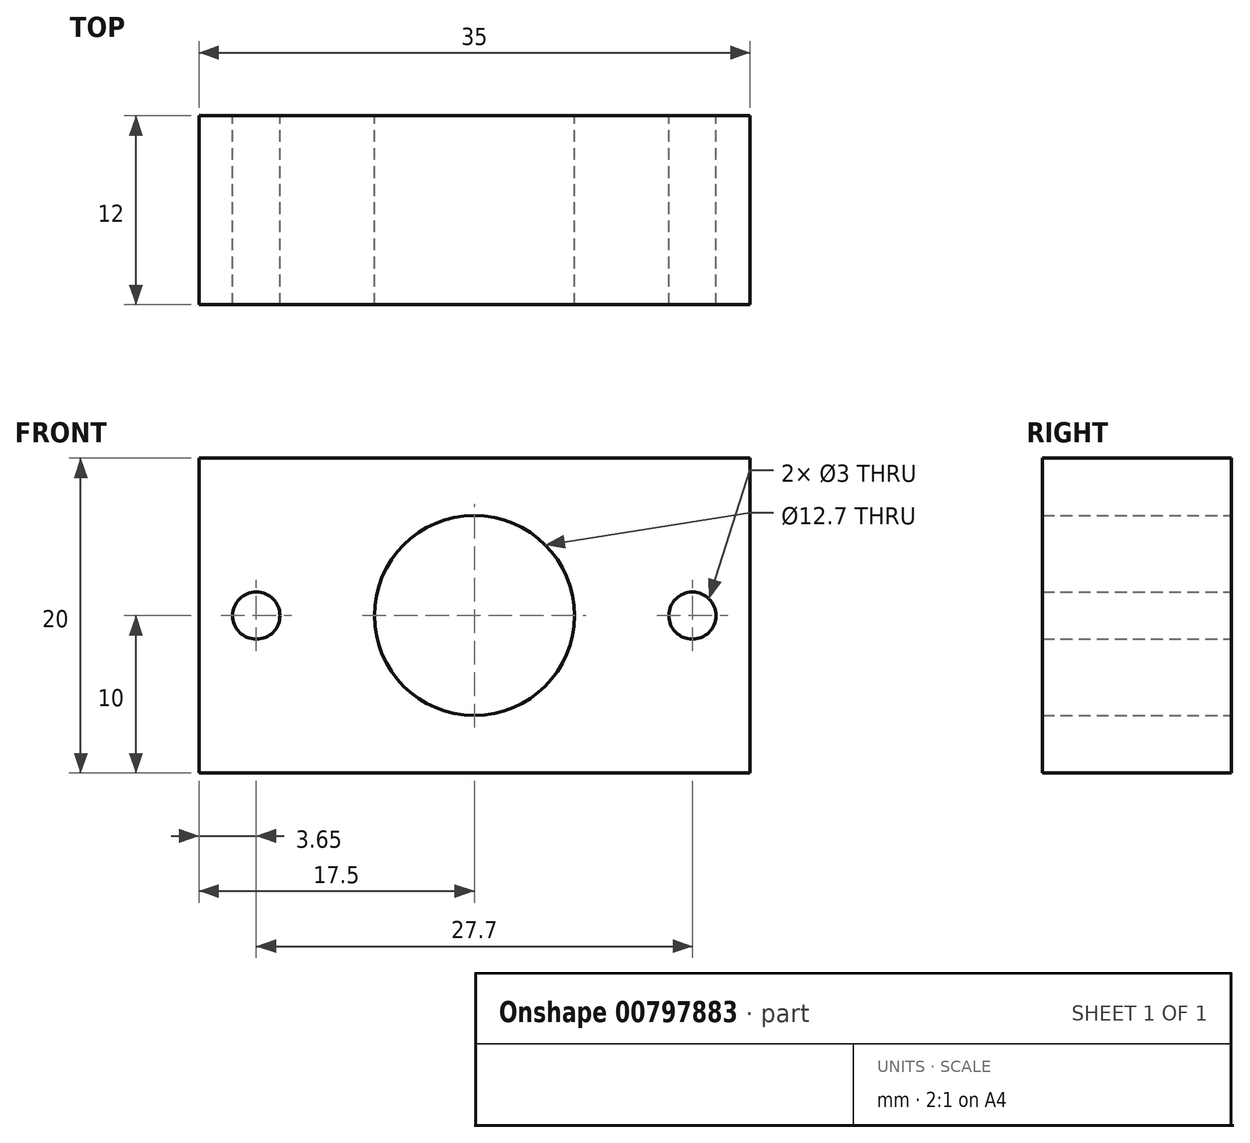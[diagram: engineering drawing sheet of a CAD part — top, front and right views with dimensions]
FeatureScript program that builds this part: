
annotation { "Feature Type Name" : "Feature", "Feature Type Description" : "" }
export const myFeature = defineFeature(function(context is Context, id is Id, definition is map)
    precondition{}
    {
        {
            var Q0;
            Q0=qCreatedBy(makeId("Front.planeOp"),FACE);
            var sketch = newSketch(context, id + "F0", { "sketchPlane" : qUnion([Q0])});
            skLineSegment(sketch, "E0.bottom", {"start": v(17.5, 10) * mm, "end": v(-17.5, 10) * mm});
            skLineSegment(sketch, "E0.top", {"start": v(17.5, -10) * mm, "end": v(-17.5, -10) * mm});
            skLineSegment(sketch, "E0.left", {"start": v(17.5, 10) * mm, "end": v(17.5, -10) * mm});
            skLineSegment(sketch, "E0.right", {"start": v(-17.5, 10) * mm, "end": v(-17.5, -10) * mm});
            skPoint(sketch, "E0.middle", {"position": v(0, 0) * mm});
            skCircle(sketch, "E1", {"center": v(0, 0) * mm, "radius": 6.35 * mm});
            skCircle(sketch, "E2", {"center": v(-13.85, 0) * mm, "radius": 1.5 * mm});
            skCircle(sketch, "E3", {"center": v(13.85, 0) * mm, "radius": 1.5 * mm});
            skSolve(sketch);
        }
        {
            var Q0;
            Q0 = qSketchRegion(id + "F0", true);
            extrude(context, id + "F1", {"entities" : qUnion([Q0]), "depth" : 12 * mm, "offsetDistance" : 25 * mm});
        }
    });
